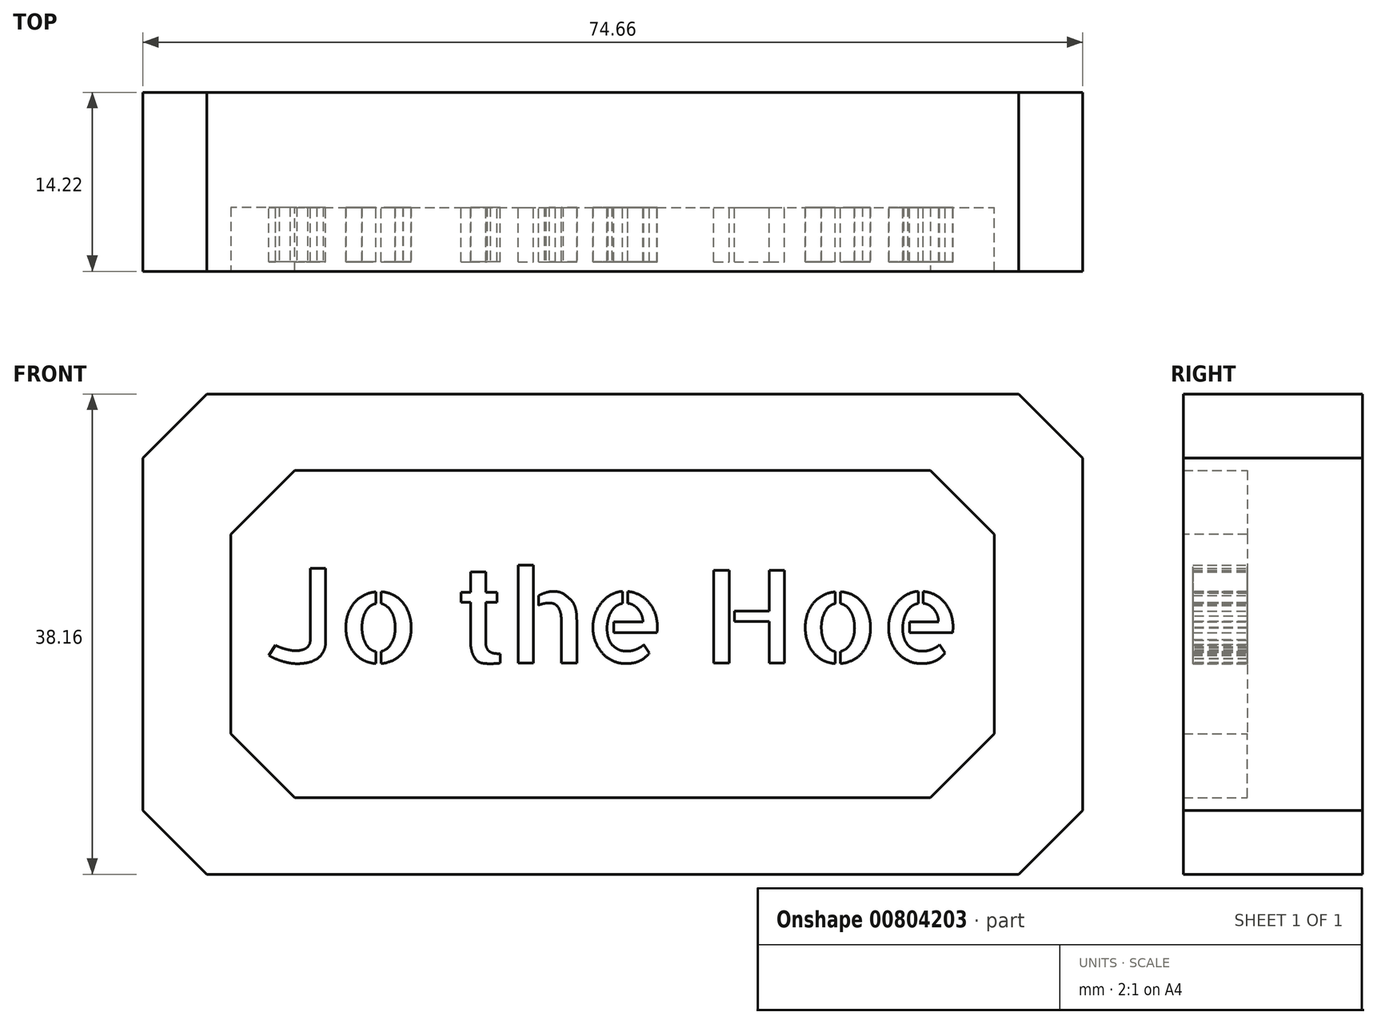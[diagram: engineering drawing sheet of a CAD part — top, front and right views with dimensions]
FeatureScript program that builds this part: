
annotation { "Feature Type Name" : "Feature", "Feature Type Description" : "" }
export const myFeature = defineFeature(function(context is Context, id is Id, definition is map)
    precondition{}
    {
        {
            var Q0;
            Q0=qCreatedBy(makeId("Front.planeOp"),FACE);
            var sketch = newSketch(context, id + "F0", { "sketchPlane" : qUnion([Q0])});
            skLineSegment(sketch, "E0.bottom", {"start": v(37.33, -19.08) * mm, "end": v(-37.33, -19.08) * mm});
            skLineSegment(sketch, "E0.top", {"start": v(37.33, 19.08) * mm, "end": v(-37.33, 19.08) * mm});
            skLineSegment(sketch, "E0.left", {"start": v(37.33, -19.08) * mm, "end": v(37.33, 19.08) * mm});
            skLineSegment(sketch, "E0.right", {"start": v(-37.33, -19.08) * mm, "end": v(-37.33, 19.08) * mm});
            skPoint(sketch, "E0.middle", {"position": v(0, 0) * mm});
            skSolve(sketch);
        }
        {
            var Q0;
            Q0=makeQuery(id+"F0.imprint","IMPRINT",FACE,{"disambiguationData":[TD([[makeQuery(id+"F0.imprint","IMPRINT",EDGE,{"derivedFrom":sQuery(id+"F0.wireOp",EDGE,"E0.bottom")}),-1.0]])]});
            var sketch = newSketch(context, id + "F1", { "sketchPlane" : qUnion([Q0])});
            skLineSegment(sketch, "E1.bottom", {"start": v(-30.33, 13) * mm, "end": v(30.33, 13) * mm});
            skLineSegment(sketch, "E1.top", {"start": v(-30.33, -13) * mm, "end": v(30.33, -13) * mm});
            skLineSegment(sketch, "E1.left", {"start": v(-30.33, 13) * mm, "end": v(-30.33, -13) * mm});
            skLineSegment(sketch, "E1.right", {"start": v(30.33, 13) * mm, "end": v(30.33, -13) * mm});
            skPoint(sketch, "E1.middle", {"position": v(0, 0) * mm});
            skSolve(sketch);
        }
        {
            var Q0;
            Q0=qCreatedBy(makeId("Front.planeOp"),FACE);
            var sketch = newSketch(context, id + "F2", { "sketchPlane" : qUnion([Q0])});
            skText(sketch, "E2", { "text": "Jo the Hoe", "fontName": "AllertaStencil-Regular.ttf"});
            const initialGuessF2  = {"E2": [-0.02756, -0.0023, 1, 0, 0.00737]};
            skSetInitialGuess(sketch, initialGuessF2);
            skSolve(sketch);
        }
        {
            var Q0;
            Q0 = qSketchRegion(id + "F2", true);
            extrude(context, id + "F3", {"entities" : qUnion([Q0]), "depth" : 4.32 * mm, "offsetDistance" : 25.4 * mm});
        }
        {
            var Q0;
            Q0 = qSketchRegion(id + "F1", true);
            extrude(context, id + "F4", {"entities" : qUnion([Q0]), "oppositeDirection" : true, "depth" : 4.32 * mm, "offsetDistance" : 25.4 * mm});
        }
        {
            var Q0;
            Q0 = qSketchRegion(id + "F0", true);
            extrude(context, id + "F5", {"entities" : qUnion([Q0]), "oppositeDirection" : true, "depth" : 9.14 * mm, "offsetDistance" : 25.4 * mm});
        }
        {
            var Q0;
            Q0=makeQuery(id+"F1.imprint","IMPRINT",FACE,{"disambiguationData":[TD([[makeQuery(id+"F1.imprint","IMPRINT",EDGE,{"derivedFrom":sQuery(id+"F1.wireOp",EDGE,"E1.bottom")}),-1.0]])]});
            extrude(context, id + "F6", {"entities" : qUnion([Q0]), "oppositeDirection" : true, "depth" : 1.78 * mm, "offsetDistance" : 25.4 * mm});
        }
        {
            var Q0;
            Q0=makeQuery(id+"F1.imprint","IMPRINT",FACE,{"disambiguationData":[TD([[makeQuery(id+"F1.imprint","IMPRINT",EDGE,{"derivedFrom":sQuery(id+"F1.wireOp",EDGE,"E1.bottom")}),1.0]])]});
            extrude(context, id + "F7", {"entities" : qUnion([Q0]), "operationType" : NewBodyOperationType.ADD, "oppositeDirection" : true, "depth" : 7.11 * mm, "offsetDistance" : 25.4 * mm});
        }
        {
            var Q0;
            Q0=makeQuery(id+"F1.imprint","IMPRINT",FACE,{"disambiguationData":[TD([[makeQuery(id+"F1.imprint","IMPRINT",EDGE,{"derivedFrom":sQuery(id+"F1.wireOp",EDGE,"E1.bottom")}),1.0]])]});
            extrude(context, id + "F8", {"entities" : qUnion([Q0]), "operationType" : NewBodyOperationType.ADD, "depth" : 5.08 * mm, "offsetDistance" : 25.4 * mm});
        }
        {
            var Q0;
            {var subQ0=sQuery(id+"F0.wireOp",EDGE,"E0.left");var subQ1=sQuery(id+"F0.wireOp",EDGE,"E0.top");Q0=makeQuery(id+"F8.boolean.opBoolean","MERGE",EDGE,{"derivedFrom":[makeQuery(id+"F5.opExtrude","SWEPT_EDGE",EDGE,{"disambiguationData":[OSD([subQ1,subQ0])]}),makeQuery(id+"F8.opExtrude","SWEPT_EDGE",EDGE,{"disambiguationData":[OSD([subQ1,subQ0])]})]});}
            var Q1;
            {var subQ0=sQuery(id+"F0.wireOp",EDGE,"E0.right");var subQ1=sQuery(id+"F0.wireOp",EDGE,"E0.top");Q1=makeQuery(id+"F8.boolean.opBoolean","MERGE",EDGE,{"derivedFrom":[makeQuery(id+"F5.opExtrude","SWEPT_EDGE",EDGE,{"disambiguationData":[OSD([subQ1,subQ0])]}),makeQuery(id+"F8.opExtrude","SWEPT_EDGE",EDGE,{"disambiguationData":[OSD([subQ1,subQ0])]})]});}
            var Q2;
            {var subQ0=sQuery(id+"F0.wireOp",EDGE,"E0.right");var subQ1=sQuery(id+"F0.wireOp",EDGE,"E0.bottom");Q2=makeQuery(id+"F8.boolean.opBoolean","MERGE",EDGE,{"derivedFrom":[makeQuery(id+"F5.opExtrude","SWEPT_EDGE",EDGE,{"disambiguationData":[OSD([subQ1,subQ0])]}),makeQuery(id+"F8.opExtrude","SWEPT_EDGE",EDGE,{"disambiguationData":[OSD([subQ1,subQ0])]})]});}
            var Q3;
            {var subQ0=sQuery(id+"F0.wireOp",EDGE,"E0.left");var subQ1=sQuery(id+"F0.wireOp",EDGE,"E0.bottom");Q3=makeQuery(id+"F8.boolean.opBoolean","MERGE",EDGE,{"derivedFrom":[makeQuery(id+"F5.opExtrude","SWEPT_EDGE",EDGE,{"disambiguationData":[OSD([subQ1,subQ0])]}),makeQuery(id+"F8.opExtrude","SWEPT_EDGE",EDGE,{"disambiguationData":[OSD([subQ1,subQ0])]})]});}
            var Q4;
            Q4=makeQuery(id+"F8.opExtrude","SWEPT_EDGE",EDGE,{"disambiguationData":[OSD([sQuery(id+"F1.wireOp",EDGE,"E1.top"),sQuery(id+"F1.wireOp",EDGE,"E1.right")])]});
            var Q5;
            Q5=makeQuery(id+"F8.opExtrude","SWEPT_EDGE",EDGE,{"disambiguationData":[OSD([sQuery(id+"F1.wireOp",EDGE,"E1.bottom"),sQuery(id+"F1.wireOp",EDGE,"E1.left")])]});
            var Q6;
            Q6=makeQuery(id+"F8.opExtrude","SWEPT_EDGE",EDGE,{"disambiguationData":[OSD([sQuery(id+"F1.wireOp",EDGE,"E1.bottom"),sQuery(id+"F1.wireOp",EDGE,"E1.right")])]});
            var Q7;
            Q7=makeQuery(id+"F8.opExtrude","SWEPT_EDGE",EDGE,{"disambiguationData":[OSD([sQuery(id+"F1.wireOp",EDGE,"E1.top"),sQuery(id+"F1.wireOp",EDGE,"E1.left")])]});
            chamfer(context, id + "F9", {"entities" : qUnion([Q0, Q1, Q2, Q3, Q4, Q5, Q6, Q7]), "width" : 5.08 * mm, "tangentPropagation" : true});
        }
    });
